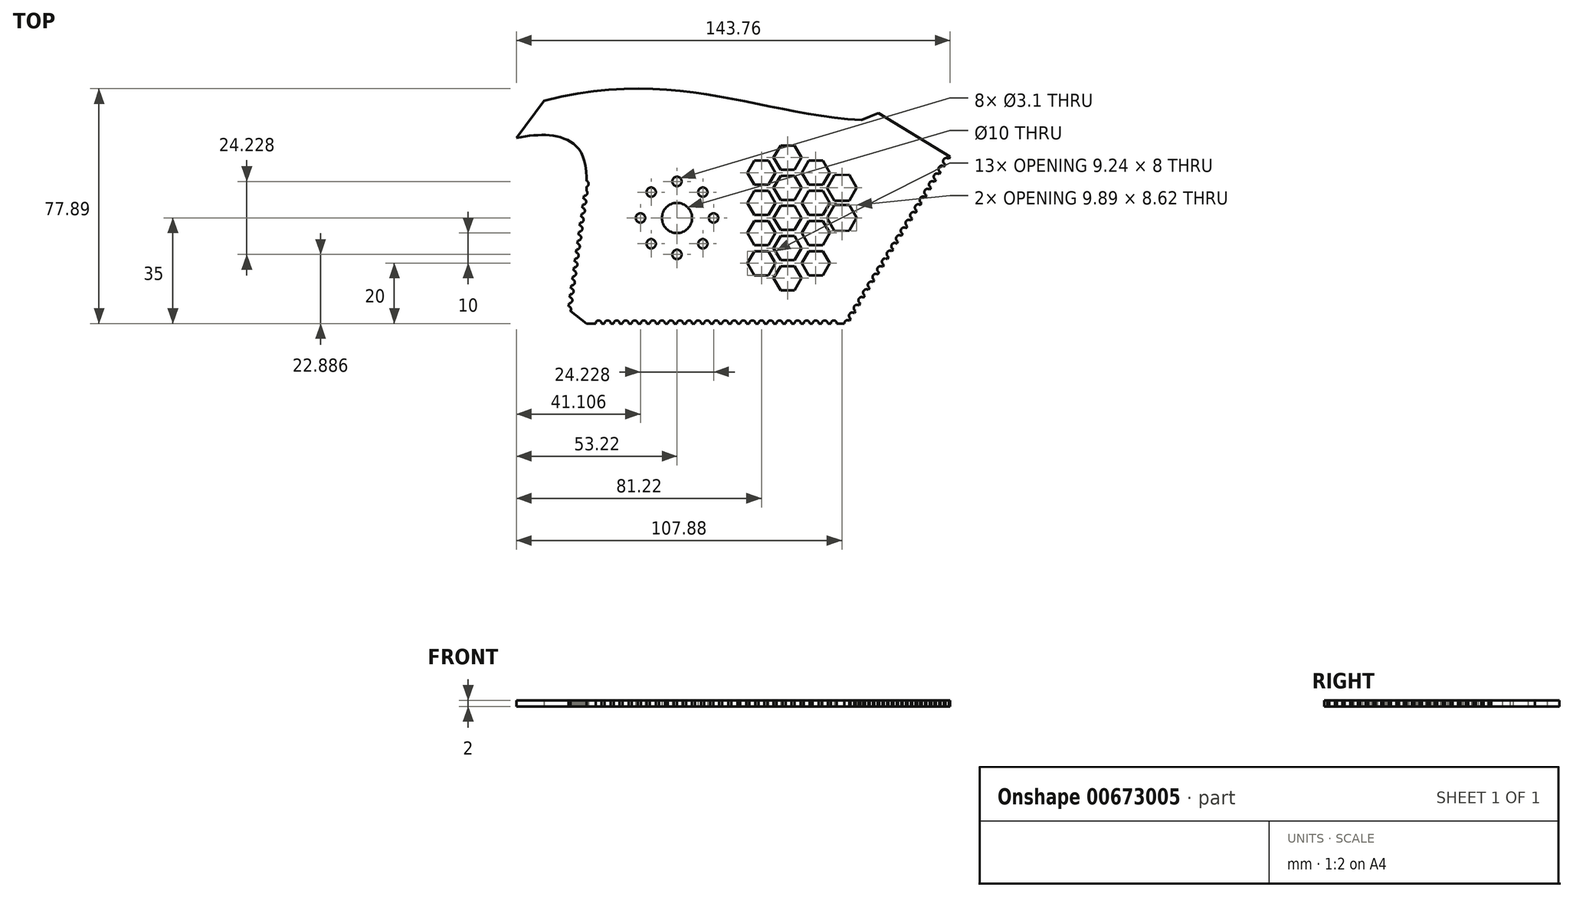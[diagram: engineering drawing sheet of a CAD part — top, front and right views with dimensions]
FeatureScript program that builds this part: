
annotation { "Feature Type Name" : "Feature", "Feature Type Description" : "" }
export const myFeature = defineFeature(function(context is Context, id is Id, definition is map)
    precondition{}
    {
        {
            var Q0;
            Q0=qCreatedBy(makeId("Top.planeOp"),FACE);
            var sketch = newSketch(context, id + "F0", { "sketchPlane" : qUnion([Q0])});
            skCircle(sketch, "E0", {"center": v(0, 0) * mm, "radius": 5 * mm});
            skCircle(sketch, "E1", {"center": v(0, 12.11) * mm, "radius": 1.55 * mm});
            skCircle(sketch, "E2.1.0", {"center": v(-8.57, 8.57) * mm, "radius": 1.55 * mm});
            skCircle(sketch, "E2.2.0", {"center": v(-12.11, 0) * mm, "radius": 1.55 * mm});
            skCircle(sketch, "E2.3.0", {"center": v(-8.57, -8.57) * mm, "radius": 1.55 * mm});
            skCircle(sketch, "E2.4.0", {"center": v(0, -12.11) * mm, "radius": 1.55 * mm});
            skCircle(sketch, "E2.5.0", {"center": v(8.57, -8.57) * mm, "radius": 1.55 * mm});
            skCircle(sketch, "E2.6.0", {"center": v(12.11, 0) * mm, "radius": 1.55 * mm});
            skCircle(sketch, "E2.7.0", {"center": v(8.57, 8.57) * mm, "radius": 1.55 * mm});
            skLineSegment(sketch, "E3.bottom", {"start": v(-30, -35) * mm, "end": v(56.58, -35) * mm});
            skLineSegment(sketch, "E3.top", {"start": v(-30, 27.38) * mm, "end": v(56.58, 27.38) * mm});
            skLineSegment(sketch, "E3.left", {"start": v(-30, -35) * mm, "end": v(-30, 27.38) * mm});
            skLineSegment(sketch, "E3.right", {"start": v(56.58, -35) * mm, "end": v(56.58, 27.38) * mm});
            skLineSegment(sketch, "E4", {"start": v(56.58, -35) * mm, "end": v(90.54, 20.31) * mm});
            skLineSegment(sketch, "E5", {"start": v(90.54, 20.31) * mm, "end": v(66.85, 34.86) * mm});
            skLineSegment(sketch, "E6", {"start": v(66.85, 34.86) * mm, "end": v(61.2, 32.47) * mm});
            skLineSegment(sketch, "E7", {"start": v(-44.07, 38.9) * mm, "end": v(-53.22, 26.57) * mm});
            skLineSegment(sketch, "E8", {"start": v(-30, 13.45) * mm, "end": v(-36.12, -30.27) * mm});
            skLineSegment(sketch, "E9", {"start": v(-36.12, -30.27) * mm, "end": v(-30, -35) * mm});
            skFitSpline(sketch, "E10", {"points": [v(-44.07, 38.9) * mm, v(61.2, 32.47) * mm], "startDerivative": vector(132.22, 33.39) * mm, "endDerivative": vector(105.27, -6.43) * mm});
            skFitSpline(sketch, "E11", {"points": [v(-53.22, 26.57) * mm, v(-38.1, 26.57) * mm, v(-30, 13.45) * mm], "startDerivative": vector(33.93, 6.5) * mm, "endDerivative": vector(0, -49.7) * mm});
            skCircle(sketch, "E12", {"center": v(-26, -35) * mm, "radius": 1 * mm});
            skCircle(sketch, "E13.1.0.0", {"center": v(-23, -35) * mm, "radius": 1 * mm});
            skCircle(sketch, "E13.2.0.0", {"center": v(-20, -35) * mm, "radius": 1 * mm});
            skCircle(sketch, "E13.3.0.0", {"center": v(-17, -35) * mm, "radius": 1 * mm});
            skCircle(sketch, "E13.4.0.0", {"center": v(-14, -35) * mm, "radius": 1 * mm});
            skCircle(sketch, "E13.5.0.0", {"center": v(-11, -35) * mm, "radius": 1 * mm});
            skCircle(sketch, "E13.6.0.0", {"center": v(-8, -35) * mm, "radius": 1 * mm});
            skCircle(sketch, "E13.7.0.0", {"center": v(-5, -35) * mm, "radius": 1 * mm});
            skCircle(sketch, "E13.8.0.0", {"center": v(-2, -35) * mm, "radius": 1 * mm});
            skCircle(sketch, "E13.9.0.0", {"center": v(1, -35) * mm, "radius": 1 * mm});
            skCircle(sketch, "E13.10.0.0", {"center": v(4, -35) * mm, "radius": 1 * mm});
            skCircle(sketch, "E13.11.0.0", {"center": v(7, -35) * mm, "radius": 1 * mm});
            skCircle(sketch, "E13.12.0.0", {"center": v(10, -35) * mm, "radius": 1 * mm});
            skCircle(sketch, "E13.13.0.0", {"center": v(13, -35) * mm, "radius": 1 * mm});
            skCircle(sketch, "E13.14.0.0", {"center": v(16, -35) * mm, "radius": 1 * mm});
            skCircle(sketch, "E13.15.0.0", {"center": v(19, -35) * mm, "radius": 1 * mm});
            skCircle(sketch, "E13.16.0.0", {"center": v(22, -35) * mm, "radius": 1 * mm});
            skCircle(sketch, "E13.17.0.0", {"center": v(25, -35) * mm, "radius": 1 * mm});
            skCircle(sketch, "E13.18.0.0", {"center": v(28, -35) * mm, "radius": 1 * mm});
            skCircle(sketch, "E13.19.0.0", {"center": v(31, -35) * mm, "radius": 1 * mm});
            skCircle(sketch, "E13.20.0.0", {"center": v(34, -35) * mm, "radius": 1 * mm});
            skCircle(sketch, "E13.21.0.0", {"center": v(37, -35) * mm, "radius": 1 * mm});
            skCircle(sketch, "E13.22.0.0", {"center": v(40, -35) * mm, "radius": 1 * mm});
            skCircle(sketch, "E13.23.0.0", {"center": v(43, -35) * mm, "radius": 1 * mm});
            skCircle(sketch, "E13.24.0.0", {"center": v(46, -35) * mm, "radius": 1 * mm});
            skCircle(sketch, "E13.25.0.0", {"center": v(49, -35) * mm, "radius": 1 * mm});
            skCircle(sketch, "E13.26.0.0", {"center": v(52, -35) * mm, "radius": 1 * mm});
            skLineSegment(sketch, "E13.direction1", {"start": v(-26, -35) * mm, "end": v(-23, -35) * mm, "construction": true});
            skCircle(sketch, "E14", {"center": v(56.58, -35) * mm, "radius": 1.1 * mm});
            skCircle(sketch, "E15.1.0.0", {"center": v(58.14, -32.44) * mm, "radius": 1.1 * mm});
            skCircle(sketch, "E15.2.0.0", {"center": v(59.7, -29.88) * mm, "radius": 1.1 * mm});
            skCircle(sketch, "E15.3.0.0", {"center": v(61.26, -27.31) * mm, "radius": 1.1 * mm});
            skCircle(sketch, "E15.4.0.0", {"center": v(62.82, -24.75) * mm, "radius": 1.1 * mm});
            skCircle(sketch, "E15.5.0.0", {"center": v(64.38, -22.19) * mm, "radius": 1.1 * mm});
            skCircle(sketch, "E15.6.0.0", {"center": v(65.94, -19.63) * mm, "radius": 1.1 * mm});
            skCircle(sketch, "E15.7.0.0", {"center": v(67.5, -17.06) * mm, "radius": 1.1 * mm});
            skCircle(sketch, "E15.8.0.0", {"center": v(69.06, -14.5) * mm, "radius": 1.1 * mm});
            skCircle(sketch, "E15.9.0.0", {"center": v(70.62, -11.94) * mm, "radius": 1.1 * mm});
            skCircle(sketch, "E15.10.0.0", {"center": v(72.18, -9.38) * mm, "radius": 1.1 * mm});
            skCircle(sketch, "E15.11.0.0", {"center": v(73.74, -6.82) * mm, "radius": 1.1 * mm});
            skCircle(sketch, "E15.12.0.0", {"center": v(75.3, -4.25) * mm, "radius": 1.1 * mm});
            skCircle(sketch, "E15.13.0.0", {"center": v(76.87, -1.7) * mm, "radius": 1.1 * mm});
            skCircle(sketch, "E15.14.0.0", {"center": v(78.43, 0.87) * mm, "radius": 1.1 * mm});
            skCircle(sketch, "E15.15.0.0", {"center": v(79.99, 3.43) * mm, "radius": 1.1 * mm});
            skCircle(sketch, "E15.16.0.0", {"center": v(81.55, 6) * mm, "radius": 1.1 * mm});
            skCircle(sketch, "E15.17.0.0", {"center": v(83.1, 8.56) * mm, "radius": 1.1 * mm});
            skCircle(sketch, "E15.18.0.0", {"center": v(84.67, 11.12) * mm, "radius": 1.1 * mm});
            skCircle(sketch, "E15.19.0.0", {"center": v(86.23, 13.68) * mm, "radius": 1.1 * mm});
            skLineSegment(sketch, "E15.direction1", {"start": v(56.58, -35) * mm, "end": v(58.14, -32.44) * mm, "construction": true});
            skCircle(sketch, "E16.0.20.0", {"center": v(87.79, 16.25) * mm, "radius": 1.1 * mm});
            skCircle(sketch, "E16.0.21.0", {"center": v(89.35, 18.8) * mm, "radius": 1.1 * mm});
            skCircle(sketch, "E17", {"center": v(-36.12, -30.27) * mm, "radius": 1 * mm});
            skCircle(sketch, "E18.1.0.0", {"center": v(-35.7, -27.3) * mm, "radius": 1 * mm});
            skCircle(sketch, "E18.2.0.0", {"center": v(-35.3, -24.33) * mm, "radius": 1 * mm});
            skCircle(sketch, "E18.3.0.0", {"center": v(-34.87, -21.36) * mm, "radius": 1 * mm});
            skCircle(sketch, "E18.4.0.0", {"center": v(-34.46, -18.39) * mm, "radius": 1 * mm});
            skCircle(sketch, "E18.5.0.0", {"center": v(-34.04, -15.41) * mm, "radius": 1 * mm});
            skCircle(sketch, "E18.6.0.0", {"center": v(-33.62, -12.44) * mm, "radius": 1 * mm});
            skCircle(sketch, "E18.7.0.0", {"center": v(-33.2, -9.47) * mm, "radius": 1 * mm});
            skCircle(sketch, "E18.8.0.0", {"center": v(-32.79, -6.5) * mm, "radius": 1 * mm});
            skCircle(sketch, "E18.9.0.0", {"center": v(-32.37, -3.53) * mm, "radius": 1 * mm});
            skCircle(sketch, "E18.10.0.0", {"center": v(-31.95, -0.56) * mm, "radius": 1 * mm});
            skCircle(sketch, "E18.11.0.0", {"center": v(-31.54, 2.41) * mm, "radius": 1 * mm});
            skCircle(sketch, "E18.12.0.0", {"center": v(-31.12, 5.38) * mm, "radius": 1 * mm});
            skCircle(sketch, "E18.13.0.0", {"center": v(-30.7, 8.35) * mm, "radius": 1 * mm});
            skCircle(sketch, "E18.14.0.0", {"center": v(-30.29, 11.32) * mm, "radius": 1 * mm});
            skLineSegment(sketch, "E18.direction1", {"start": v(-36.12, -30.27) * mm, "end": v(-35.7, -27.3) * mm, "construction": true});
            skCircle(sketch, "E19.cCircle", {"center": v(28, -15) * mm, "radius": 4 * mm, "construction": true});
            skLineSegment(sketch, "E19.0", {"start": v(32.62, -15) * mm, "end": v(30.3, -19) * mm});
            skLineSegment(sketch, "E19.1", {"start": v(30.3, -19) * mm, "end": v(25.7, -19) * mm});
            skLineSegment(sketch, "E19.2", {"start": v(25.7, -19) * mm, "end": v(23.38, -15) * mm});
            skLineSegment(sketch, "E19.3", {"start": v(23.38, -15) * mm, "end": v(25.7, -11) * mm});
            skLineSegment(sketch, "E19.4", {"start": v(25.7, -11) * mm, "end": v(30.3, -11) * mm});
            skLineSegment(sketch, "E19.5", {"start": v(30.3, -11) * mm, "end": v(32.62, -15) * mm});
            skPoint(sketch, "E19.0.midPoint", {"position": v(31.46, -17) * mm});
            skLineSegment(sketch, "E20.0.1.0", {"start": v(30.3, -9) * mm, "end": v(25.7, -9) * mm});
            skPoint(sketch, "E20.0.1.1", {"position": v(31.46, -7) * mm});
            skLineSegment(sketch, "E20.0.1.2", {"start": v(30.3, -1) * mm, "end": v(32.62, -5) * mm});
            skLineSegment(sketch, "E20.0.1.3", {"start": v(25.7, -9) * mm, "end": v(23.38, -5) * mm});
            skCircle(sketch, "E20.0.1.4", {"center": v(28, -5) * mm, "radius": 4 * mm, "construction": true});
            skLineSegment(sketch, "E20.0.1.5", {"start": v(23.38, -5) * mm, "end": v(25.7, -1) * mm});
            skLineSegment(sketch, "E20.0.1.6", {"start": v(25.7, -1) * mm, "end": v(30.3, -1) * mm});
            skLineSegment(sketch, "E20.0.1.7", {"start": v(32.62, -5) * mm, "end": v(30.3, -9) * mm});
            skLineSegment(sketch, "E20.0.2.0", {"start": v(30.3, 1) * mm, "end": v(25.7, 1) * mm});
            skPoint(sketch, "E20.0.2.1", {"position": v(31.46, 3) * mm});
            skLineSegment(sketch, "E20.0.2.2", {"start": v(30.3, 9) * mm, "end": v(32.62, 5) * mm});
            skLineSegment(sketch, "E20.0.2.3", {"start": v(25.7, 1) * mm, "end": v(23.38, 5) * mm});
            skCircle(sketch, "E20.0.2.4", {"center": v(28, 5) * mm, "radius": 4 * mm, "construction": true});
            skLineSegment(sketch, "E20.0.2.5", {"start": v(23.38, 5) * mm, "end": v(25.7, 9) * mm});
            skLineSegment(sketch, "E20.0.2.6", {"start": v(25.7, 9) * mm, "end": v(30.3, 9) * mm});
            skLineSegment(sketch, "E20.0.2.7", {"start": v(32.62, 5) * mm, "end": v(30.3, 1) * mm});
            skLineSegment(sketch, "E20.0.3.0", {"start": v(30.3, 11) * mm, "end": v(25.7, 11) * mm});
            skPoint(sketch, "E20.0.3.1", {"position": v(31.46, 13) * mm});
            skLineSegment(sketch, "E20.0.3.2", {"start": v(30.3, 19) * mm, "end": v(32.62, 15) * mm});
            skLineSegment(sketch, "E20.0.3.3", {"start": v(25.7, 11) * mm, "end": v(23.38, 15) * mm});
            skCircle(sketch, "E20.0.3.4", {"center": v(28, 15) * mm, "radius": 4 * mm, "construction": true});
            skLineSegment(sketch, "E20.0.3.5", {"start": v(23.38, 15) * mm, "end": v(25.7, 19) * mm});
            skLineSegment(sketch, "E20.0.3.6", {"start": v(25.7, 19) * mm, "end": v(30.3, 19) * mm});
            skLineSegment(sketch, "E20.0.3.7", {"start": v(32.62, 15) * mm, "end": v(30.3, 11) * mm});
            skLineSegment(sketch, "E20.direction1", {"start": v(25.7, -19) * mm, "end": v(43.7, -19) * mm, "construction": true});
            skLineSegment(sketch, "E20.direction2", {"start": v(25.7, -19) * mm, "end": v(25.7, -9) * mm, "construction": true});
            skCircle(sketch, "E21.cCircle", {"center": v(36.66, -20) * mm, "radius": 4 * mm, "construction": true});
            skLineSegment(sketch, "E21.0", {"start": v(41.28, -20) * mm, "end": v(38.97, -24) * mm});
            skLineSegment(sketch, "E21.1", {"start": v(38.97, -24) * mm, "end": v(34.35, -24) * mm});
            skLineSegment(sketch, "E21.2", {"start": v(34.35, -24) * mm, "end": v(32.04, -20) * mm});
            skLineSegment(sketch, "E21.3", {"start": v(32.04, -20) * mm, "end": v(34.35, -16) * mm});
            skLineSegment(sketch, "E21.4", {"start": v(34.35, -16) * mm, "end": v(38.97, -16) * mm});
            skLineSegment(sketch, "E21.5", {"start": v(38.97, -16) * mm, "end": v(41.28, -20) * mm});
            skPoint(sketch, "E21.0.midPoint", {"position": v(40.12, -22) * mm});
            skLineSegment(sketch, "E22.0.1.0", {"start": v(32.04, -10) * mm, "end": v(34.35, -6) * mm});
            skLineSegment(sketch, "E22.0.1.1", {"start": v(34.35, -6) * mm, "end": v(38.97, -6) * mm});
            skLineSegment(sketch, "E22.0.1.2", {"start": v(38.97, -6) * mm, "end": v(41.28, -10) * mm});
            skLineSegment(sketch, "E22.0.1.3", {"start": v(41.28, -10) * mm, "end": v(38.97, -14) * mm});
            skLineSegment(sketch, "E22.0.1.4", {"start": v(38.97, -14) * mm, "end": v(34.35, -14) * mm});
            skLineSegment(sketch, "E22.0.1.5", {"start": v(34.35, -14) * mm, "end": v(32.04, -10) * mm});
            skLineSegment(sketch, "E22.0.2.0", {"start": v(32.04, 0) * mm, "end": v(34.35, 4) * mm});
            skLineSegment(sketch, "E22.0.2.1", {"start": v(34.35, 4) * mm, "end": v(38.97, 4) * mm});
            skLineSegment(sketch, "E22.0.2.2", {"start": v(38.97, 4) * mm, "end": v(41.28, 0) * mm});
            skLineSegment(sketch, "E22.0.2.3", {"start": v(41.28, 0) * mm, "end": v(38.97, -4) * mm});
            skLineSegment(sketch, "E22.0.2.4", {"start": v(38.97, -4) * mm, "end": v(34.35, -4) * mm});
            skLineSegment(sketch, "E22.0.2.5", {"start": v(34.35, -4) * mm, "end": v(32.04, 0) * mm});
            skLineSegment(sketch, "E22.0.3.0", {"start": v(32.04, 10) * mm, "end": v(34.35, 14) * mm});
            skLineSegment(sketch, "E22.0.3.1", {"start": v(34.35, 14) * mm, "end": v(38.97, 14) * mm});
            skLineSegment(sketch, "E22.0.3.2", {"start": v(38.97, 14) * mm, "end": v(41.28, 10) * mm});
            skLineSegment(sketch, "E22.0.3.3", {"start": v(41.28, 10) * mm, "end": v(38.97, 6) * mm});
            skLineSegment(sketch, "E22.0.3.4", {"start": v(38.97, 6) * mm, "end": v(34.35, 6) * mm});
            skLineSegment(sketch, "E22.0.3.5", {"start": v(34.35, 6) * mm, "end": v(32.04, 10) * mm});
            skLineSegment(sketch, "E22.0.4.0", {"start": v(32.04, 20) * mm, "end": v(34.35, 24) * mm});
            skLineSegment(sketch, "E22.0.4.1", {"start": v(34.35, 24) * mm, "end": v(38.97, 24) * mm});
            skLineSegment(sketch, "E22.0.4.2", {"start": v(38.97, 24) * mm, "end": v(41.28, 20) * mm});
            skLineSegment(sketch, "E22.0.4.3", {"start": v(41.28, 20) * mm, "end": v(38.97, 16) * mm});
            skLineSegment(sketch, "E22.0.4.4", {"start": v(38.97, 16) * mm, "end": v(34.35, 16) * mm});
            skLineSegment(sketch, "E22.0.4.5", {"start": v(34.35, 16) * mm, "end": v(32.04, 20) * mm});
            skLineSegment(sketch, "E22.direction1", {"start": v(32.04, -20) * mm, "end": v(53.32, -20) * mm, "construction": true});
            skLineSegment(sketch, "E22.direction2", {"start": v(32.04, -20) * mm, "end": v(32.04, -10) * mm, "construction": true});
            skLineSegment(sketch, "E23.0.1.0", {"start": v(48.3, -19) * mm, "end": v(43.7, -19) * mm});
            skPoint(sketch, "E23.3.1.0", {"position": v(49.46, -17) * mm});
            skLineSegment(sketch, "E23.4.1.0", {"start": v(48.3, -11) * mm, "end": v(50.62, -15) * mm});
            skLineSegment(sketch, "E23.7.1.0", {"start": v(43.7, -19) * mm, "end": v(41.38, -15) * mm});
            skCircle(sketch, "E23.10.1.0", {"center": v(46, -15) * mm, "radius": 4 * mm, "construction": true});
            skLineSegment(sketch, "E23.12.1.0", {"start": v(41.38, -15) * mm, "end": v(43.7, -11) * mm});
            skLineSegment(sketch, "E23.15.1.0", {"start": v(43.7, -11) * mm, "end": v(48.3, -11) * mm});
            skLineSegment(sketch, "E23.18.1.0", {"start": v(50.62, -15) * mm, "end": v(48.3, -19) * mm});
            skLineSegment(sketch, "E23.0.1.1", {"start": v(48.3, -9) * mm, "end": v(43.7, -9) * mm});
            skPoint(sketch, "E23.3.1.1", {"position": v(49.46, -7) * mm});
            skLineSegment(sketch, "E23.4.1.1", {"start": v(48.3, -1) * mm, "end": v(50.62, -5) * mm});
            skLineSegment(sketch, "E23.7.1.1", {"start": v(43.7, -9) * mm, "end": v(41.38, -5) * mm});
            skCircle(sketch, "E23.10.1.1", {"center": v(46, -5) * mm, "radius": 4 * mm, "construction": true});
            skLineSegment(sketch, "E23.12.1.1", {"start": v(41.38, -5) * mm, "end": v(43.7, -1) * mm});
            skLineSegment(sketch, "E23.15.1.1", {"start": v(43.7, -1) * mm, "end": v(48.3, -1) * mm});
            skLineSegment(sketch, "E23.18.1.1", {"start": v(50.62, -5) * mm, "end": v(48.3, -9) * mm});
            skLineSegment(sketch, "E23.0.1.2", {"start": v(48.3, 1) * mm, "end": v(43.7, 1) * mm});
            skPoint(sketch, "E23.3.1.2", {"position": v(49.46, 3) * mm});
            skLineSegment(sketch, "E23.4.1.2", {"start": v(48.3, 9) * mm, "end": v(50.62, 5) * mm});
            skLineSegment(sketch, "E23.7.1.2", {"start": v(43.7, 1) * mm, "end": v(41.38, 5) * mm});
            skCircle(sketch, "E23.10.1.2", {"center": v(46, 5) * mm, "radius": 4 * mm, "construction": true});
            skLineSegment(sketch, "E23.12.1.2", {"start": v(41.38, 5) * mm, "end": v(43.7, 9) * mm});
            skLineSegment(sketch, "E23.15.1.2", {"start": v(43.7, 9) * mm, "end": v(48.3, 9) * mm});
            skLineSegment(sketch, "E23.18.1.2", {"start": v(50.62, 5) * mm, "end": v(48.3, 1) * mm});
            skLineSegment(sketch, "E23.0.1.3", {"start": v(48.3, 11) * mm, "end": v(43.7, 11) * mm});
            skPoint(sketch, "E23.3.1.3", {"position": v(49.46, 13) * mm});
            skLineSegment(sketch, "E23.4.1.3", {"start": v(48.3, 19) * mm, "end": v(50.62, 15) * mm});
            skLineSegment(sketch, "E23.7.1.3", {"start": v(43.7, 11) * mm, "end": v(41.38, 15) * mm});
            skCircle(sketch, "E23.10.1.3", {"center": v(46, 15) * mm, "radius": 4 * mm, "construction": true});
            skLineSegment(sketch, "E23.12.1.3", {"start": v(41.38, 15) * mm, "end": v(43.7, 19) * mm});
            skLineSegment(sketch, "E23.15.1.3", {"start": v(43.7, 19) * mm, "end": v(48.3, 19) * mm});
            skLineSegment(sketch, "E23.18.1.3", {"start": v(50.62, 15) * mm, "end": v(48.3, 11) * mm});
            skCircle(sketch, "E24.cCircle", {"center": v(54.66, 10) * mm, "radius": 4.28 * mm, "construction": true});
            skLineSegment(sketch, "E24.0", {"start": v(59.6, 10.06) * mm, "end": v(57.19, 5.75) * mm});
            skLineSegment(sketch, "E24.1", {"start": v(57.19, 5.75) * mm, "end": v(52.24, 5.69) * mm});
            skLineSegment(sketch, "E24.2", {"start": v(52.24, 5.69) * mm, "end": v(49.72, 9.94) * mm});
            skLineSegment(sketch, "E24.3", {"start": v(49.72, 9.94) * mm, "end": v(52.14, 14.25) * mm});
            skLineSegment(sketch, "E24.4", {"start": v(52.14, 14.25) * mm, "end": v(57.08, 14.31) * mm});
            skLineSegment(sketch, "E24.5", {"start": v(57.08, 14.31) * mm, "end": v(59.6, 10.06) * mm});
            skPoint(sketch, "E24.0.midPoint", {"position": v(58.4, 7.9) * mm});
            skCircle(sketch, "E25.0.1.0", {"center": v(54.66, 0) * mm, "radius": 4.28 * mm, "construction": true});
            skLineSegment(sketch, "E25.0.1.1", {"start": v(52.24, -4.31) * mm, "end": v(49.72, -0.06) * mm});
            skLineSegment(sketch, "E25.0.1.2", {"start": v(52.14, 4.25) * mm, "end": v(57.08, 4.31) * mm});
            skLineSegment(sketch, "E25.0.1.3", {"start": v(57.08, 4.31) * mm, "end": v(59.6, 0.06) * mm});
            skPoint(sketch, "E25.0.1.4", {"position": v(58.4, -2.1) * mm});
            skLineSegment(sketch, "E25.0.1.5", {"start": v(56.58, -45) * mm, "end": v(56.58, 17.38) * mm});
            skLineSegment(sketch, "E25.0.1.6", {"start": v(59.6, 0.06) * mm, "end": v(57.19, -4.25) * mm});
            skLineSegment(sketch, "E25.0.1.7", {"start": v(57.19, -4.25) * mm, "end": v(52.24, -4.31) * mm});
            skLineSegment(sketch, "E25.0.1.8", {"start": v(49.72, -0.06) * mm, "end": v(52.14, 4.25) * mm});
            skLineSegment(sketch, "E25.direction1", {"start": v(56.58, -35) * mm, "end": v(81.58, -35) * mm, "construction": true});
            skLineSegment(sketch, "E25.direction2", {"start": v(56.58, -35) * mm, "end": v(56.58, -45) * mm, "construction": true});
            skSolve(sketch);
        }
        {
            var Q0;
            Q0=makeQuery(id+"F0.imprint","IMPRINT",FACE,{"disambiguationData":[TD([[makeQuery(id+"F0.imprint","IMPRINT",EDGE,{"derivedFrom":sQuery(id+"F0.wireOp",EDGE,"E0")}),-1.0]])]});
            var Q1;
            {var subQ1=sQuery(id+"F0.wireOp",EDGE,"E3.top");Q1=makeQuery(id+"F0.imprint","IMPRINT",FACE,{"disambiguationData":[TD([[makeQuery(id+"F0.imprint","IMPRINT",EDGE,{"derivedFrom":subQ1}),1.0]])]});}
            var Q2;
            {var subQ1=sQuery(id+"F0.wireOp",EDGE,"E8");var subQ32=sQuery(id+"F0.wireOp",EDGE,"E18.13.0.0");var subQ33=makeQuery(id+"F0.imprint","INTERSECT",VERTEX,{"disambiguationData":[OD(1.0)],"derivedFrom":[subQ1,subQ32]});Q2=makeQuery(id+"F0.imprint","IMPRINT",FACE,{"disambiguationData":[TD([[makeQuery(id+"F0.imprint","IMPRINT",EDGE,{"disambiguationData":[TD([[subQ33,-1.0]])],"derivedFrom":subQ1}),1.0]])]});}
            extrude(context, id + "F1", {"entities" : qUnion([Q0, Q1, Q2]), "depth" : 2 * mm, "offsetDistance" : 25 * mm});
        }
    });
